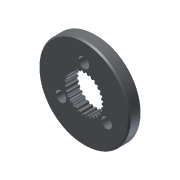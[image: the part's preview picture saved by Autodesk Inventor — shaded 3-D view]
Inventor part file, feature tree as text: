
AUTODESK INVENTOR PART (.ipt)
format: ipt  version: 2013 (Build 170138000, 138)  size: 225,792 bytes
history: native  units: in
note: dims shown in document units (in); Inventor stores cm internally (conversion verified against a paired STEP export)
features: chamfer x1, other x1, imported_body x1
ambient origin geometry x8: Origin, YZ Plane, XZ Plane, XY Plane, X Axis, Y Axis, Z Axis, Center Point
feature tree (3):
  chamfer  "Chamfer1"  [1 undecoded]
  other  "217-2625-008 Rev11"
  imported_body  "Base1"
note: 1 required parameter value undecoded (feature->parameter linkage not recoverable at this tier; creation-order binding heuristic only, values carry confidence <= 0.55)
